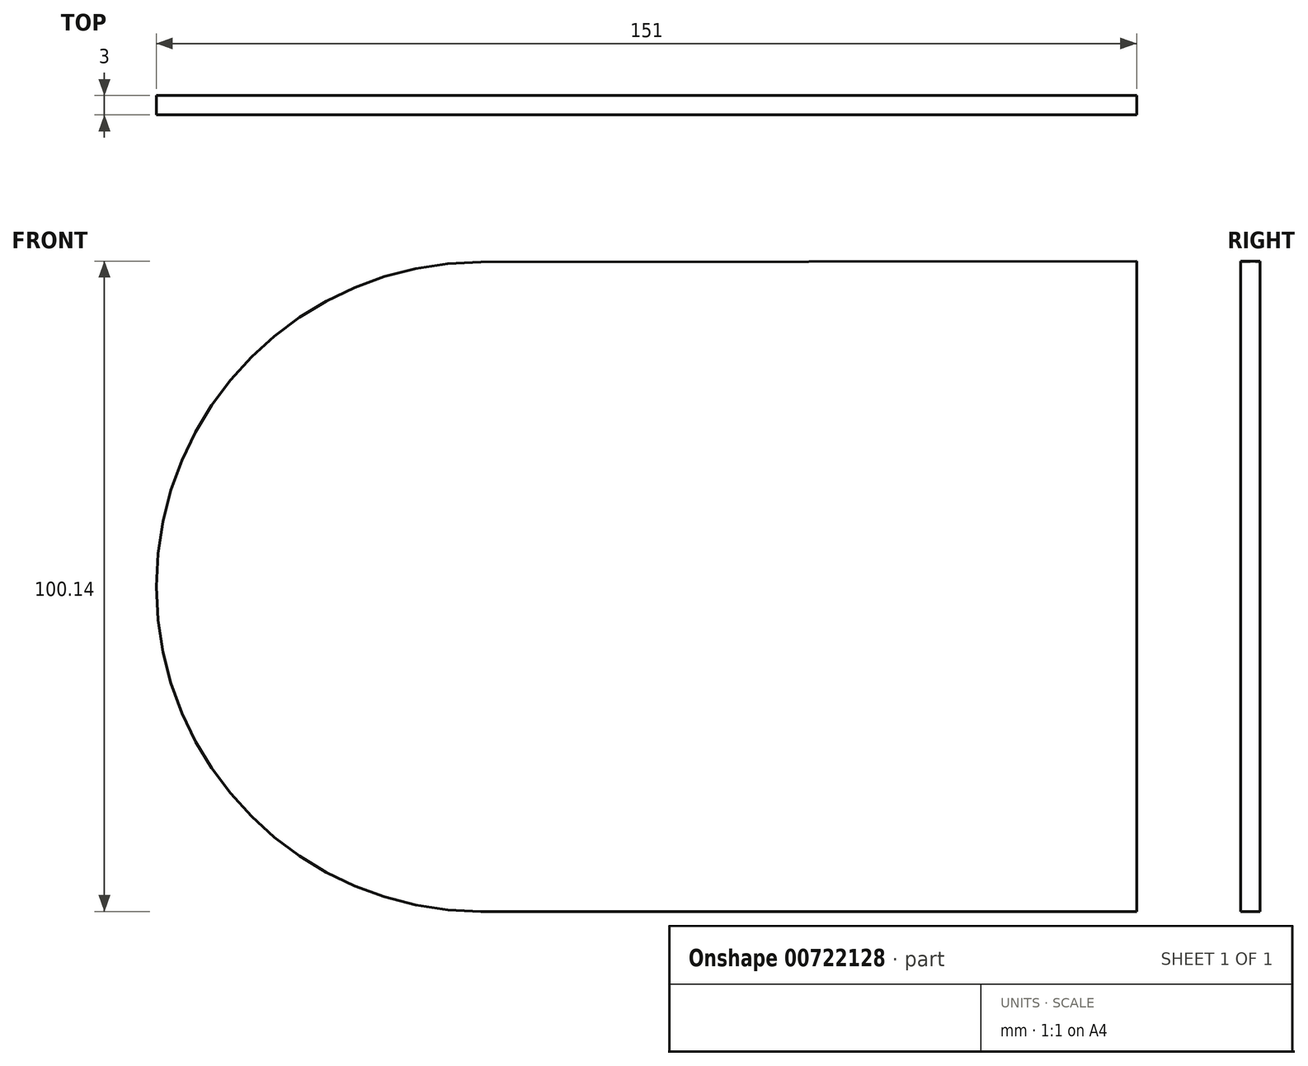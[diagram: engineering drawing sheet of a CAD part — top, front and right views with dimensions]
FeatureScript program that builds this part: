
annotation { "Feature Type Name" : "Feature", "Feature Type Description" : "" }
export const myFeature = defineFeature(function(context is Context, id is Id, definition is map)
    precondition{}
    {
        {
            var Q0;
            Q0=qCreatedBy(makeId("Front.planeOp"),FACE);
            var sketch = newSketch(context, id + "F0", { "sketchPlane" : qUnion([Q0])});
            skArc(sketch, "E0", {"start": v(-122.73, 57.97) * mm, "mid": v(-172.73, 7.97) * mm, "end": v(-122.73, -42.03) * mm});
            skLineSegment(sketch, "E1", {"start": v(-122.73, -42.03) * mm, "end": v(-21.73, -42.03) * mm});
            skLineSegment(sketch, "E2", {"start": v(-21.73, -42.03) * mm, "end": v(-21.73, 57.97) * mm});
            skPoint(sketch, "E3.end.orphan", {"position": v(-172.73, 7.97) * mm});
            skPoint(sketch, "E4.start.orphan", {"position": v(-21.73, 7.97) * mm});
            skLineSegment(sketch, "E5.trimOffspring", {"start": v(-21.73, 57.97) * mm, "end": v(-21.73, 58.11) * mm});
            skPoint(sketch, "E6.end.orphan", {"position": v(-62.73, 92.97) * mm});
            skPoint(sketch, "E7.end.orphan", {"position": v(-62.73, 57.97) * mm});
            skLineSegment(sketch, "E8", {"start": v(-21.73, 58.11) * mm, "end": v(-122.73, 57.97) * mm});
            skSolve(sketch);
        }
        {
            var Q0;
            Q0=qSketchRegion(id+"F0",true);
            extrude(context, id + "F1", {"entities" : qUnion([Q0]), "depth" : 3 * mm, "offsetDistance" : 25 * mm});
        }
    });
